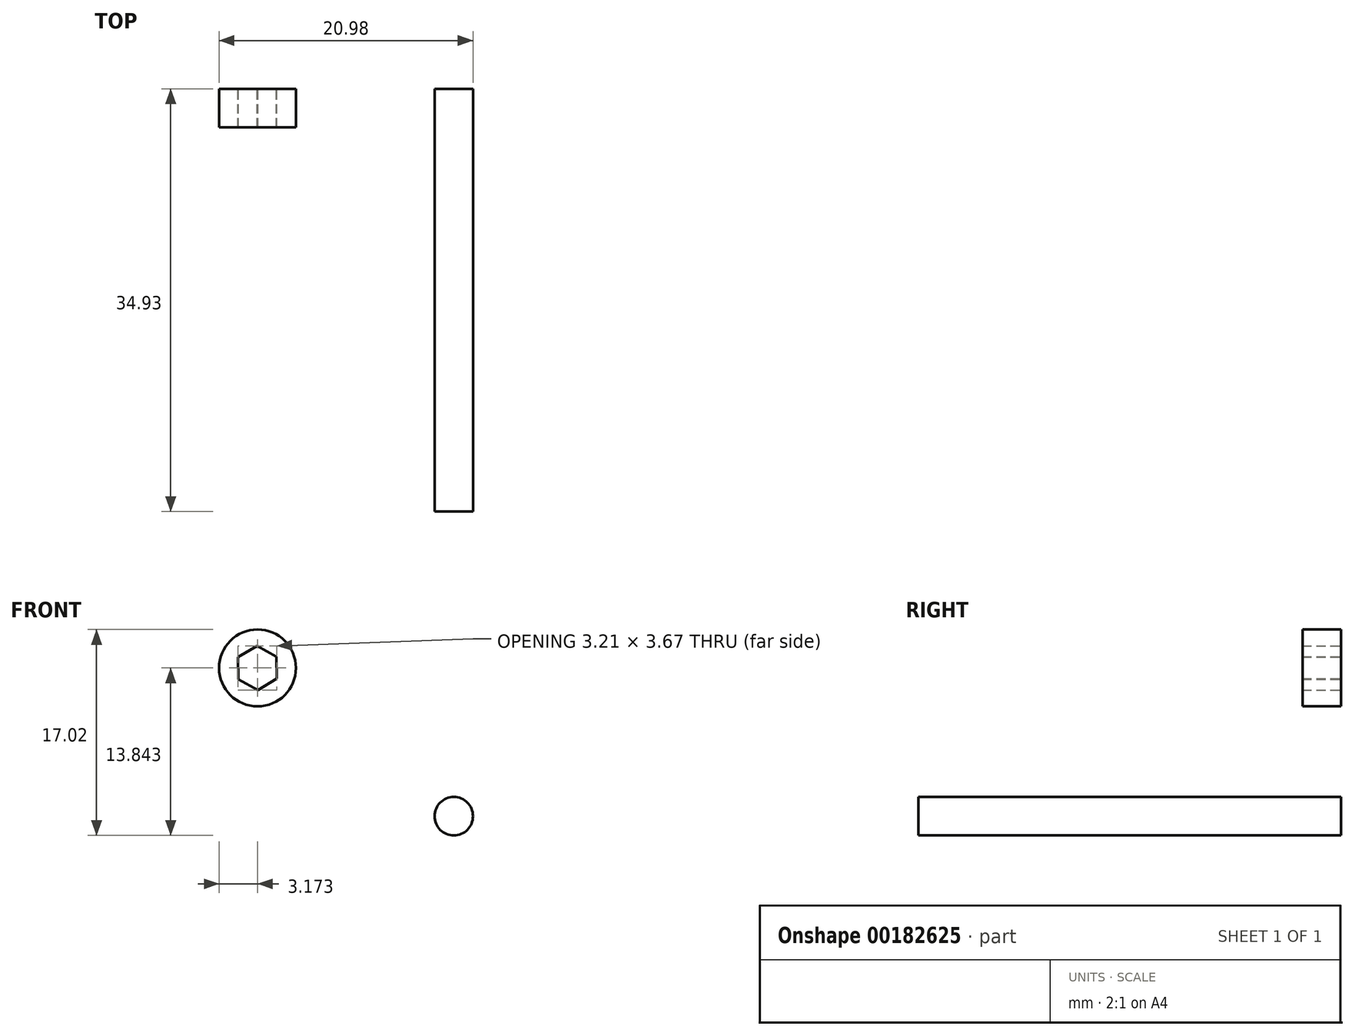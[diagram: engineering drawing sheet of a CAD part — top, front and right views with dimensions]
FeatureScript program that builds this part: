
annotation { "Feature Type Name" : "Feature", "Feature Type Description" : "" }
export const myFeature = defineFeature(function(context is Context, id is Id, definition is map)
    precondition{}
    {
        {
            var Q0;
            Q0=qCreatedBy(makeId("Front.planeOp"),FACE);
            var sketch = newSketch(context, id + "F0", { "sketchPlane" : qUnion([Q0])});
            skCircle(sketch, "E0", {"center": v(-60.36, 51.14) * mm, "radius": 3.18 * mm});
            skPoint(sketch, "E1.0.midPoint", {"position": v(-61.6, 50.4) * mm});
            skCircle(sketch, "E2.cCircle", {"center": v(-60.36, 51.14) * mm, "radius": 1.59 * mm, "construction": true});
            skLineSegment(sketch, "E2.0", {"start": v(-60.39, 52.98) * mm, "end": v(-58.78, 52.09) * mm});
            skLineSegment(sketch, "E2.1", {"start": v(-58.78, 52.09) * mm, "end": v(-58.75, 50.25) * mm});
            skLineSegment(sketch, "E2.2", {"start": v(-58.75, 50.25) * mm, "end": v(-60.33, 49.3) * mm});
            skLineSegment(sketch, "E2.3", {"start": v(-60.33, 49.3) * mm, "end": v(-61.93, 50.2) * mm});
            skLineSegment(sketch, "E2.4", {"start": v(-61.93, 50.2) * mm, "end": v(-61.96, 52.03) * mm});
            skLineSegment(sketch, "E2.5", {"start": v(-61.96, 52.03) * mm, "end": v(-60.39, 52.98) * mm});
            skPoint(sketch, "E2.0.midPoint", {"position": v(-59.59, 52.53) * mm});
            skSolve(sketch);
        }
        {
            var Q0;
            Q0=makeQuery(id+"F0.imprint","IMPRINT",FACE,{"disambiguationData":[TD([[makeQuery(id+"F0.imprint","IMPRINT",EDGE,{"derivedFrom":sQuery(id+"F0.wireOp",EDGE,"E0")}),1.0]])]});
            extrude(context, id + "F1", {"entities" : qUnion([Q0]), "depth" : 3.17 * mm});
        }
        {
            var Q0;
            Q0=qCreatedBy(makeId("Front.planeOp"),FACE);
            var sketch = newSketch(context, id + "F2", { "sketchPlane" : qUnion([Q0])});
            skCircle(sketch, "E3", {"center": v(-44.14, 38.9) * mm, "radius": 1.59 * mm});
            skSolve(sketch);
        }
        {
            var Q0;
            Q0=makeQuery(id+"F2.imprint","IMPRINT",FACE,{"disambiguationData":[TD([[makeQuery(id+"F2.imprint","IMPRINT",EDGE,{"derivedFrom":sQuery(id+"F2.wireOp",EDGE,"E3")}),1.0]])]});
            extrude(context, id + "F3", {"entities" : qUnion([Q0]), "depth" : 34.92 * mm});
        }
    });
